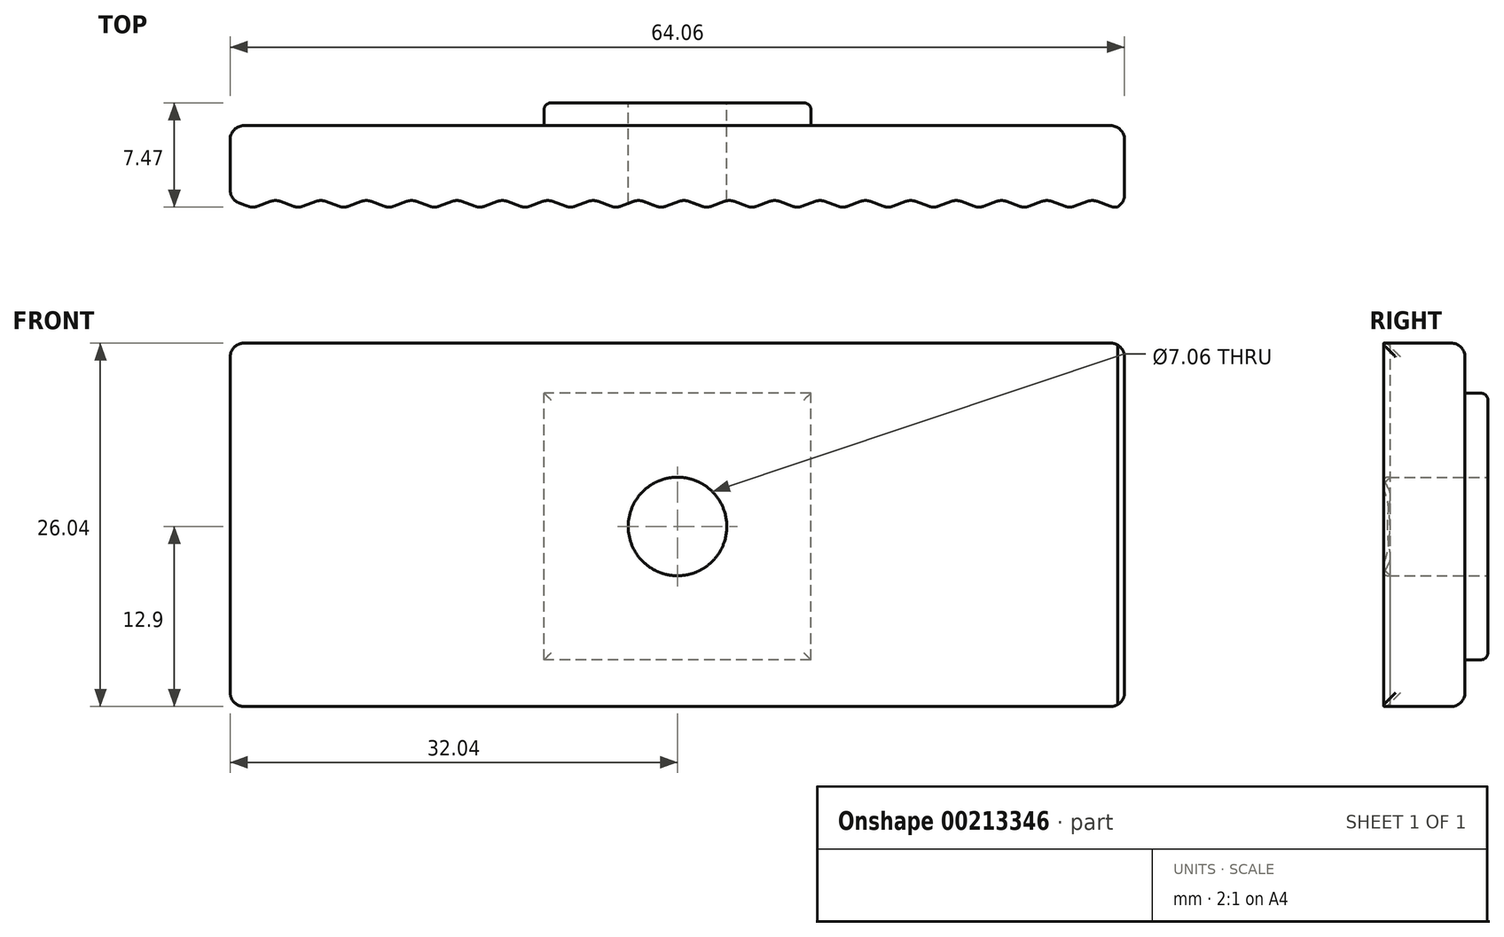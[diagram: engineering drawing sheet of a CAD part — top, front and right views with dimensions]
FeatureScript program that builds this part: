
annotation { "Feature Type Name" : "Feature", "Feature Type Description" : "" }
export const myFeature = defineFeature(function(context is Context, id is Id, definition is map)
    precondition{}
    {
        {
            var Q0;
            Q0=qCreatedBy(makeId("Front.planeOp"),FACE);
            var sketch = newSketch(context, id + "F0", { "sketchPlane" : qUnion([Q0])});
            skLineSegment(sketch, "E0.bottom", {"start": v(0, 0) * mm, "end": v(64.06, 0) * mm});
            skLineSegment(sketch, "E0.top", {"start": v(0, 26.04) * mm, "end": v(64.06, 26.04) * mm});
            skLineSegment(sketch, "E0.left", {"start": v(0, 0) * mm, "end": v(0, 26.04) * mm});
            skLineSegment(sketch, "E0.right", {"start": v(64.06, 0) * mm, "end": v(64.06, 26.04) * mm});
            skCircle(sketch, "E1", {"center": v(32.04, 12.9) * mm, "radius": 3.53 * mm});
            skSolve(sketch);
        }
        {
            var Q0;
            Q0 = qSketchRegion(id + "F0", true);
            extrude(context, id + "F1", {"entities" : qUnion([Q0]), "depth" : 5.3 * mm});
        }
        {
            var Q0;
            Q0=makeQuery(id+"F1.opExtrude","CAP_FACE",FACE,{"disambiguationData":[OSD([sQuery(id+"F0.wireOp",EDGE,"E0.bottom"),sQuery(id+"F0.wireOp",EDGE,"E0.top"),sQuery(id+"F0.wireOp",EDGE,"E0.left"),sQuery(id+"F0.wireOp",EDGE,"E0.right"),sQuery(id+"F0.wireOp",EDGE,"E1")])],"isStart":true});
            var sketch = newSketch(context, id + "F2", { "sketchPlane" : qUnion([Q0])});
            skLineSegment(sketch, "E2.bottom", {"start": v(-41.6, 3.35) * mm, "end": v(-22.48, 3.35) * mm});
            skLineSegment(sketch, "E2.top", {"start": v(-41.6, 22.46) * mm, "end": v(-22.48, 22.46) * mm});
            skLineSegment(sketch, "E2.left", {"start": v(-41.6, 3.35) * mm, "end": v(-41.6, 22.46) * mm});
            skLineSegment(sketch, "E2.right", {"start": v(-22.48, 3.35) * mm, "end": v(-22.49, 22.46) * mm});
            skCircle(sketch, "E3.0", {"center": v(-32.04, 12.9) * mm, "radius": 3.53 * mm});
            skSolve(sketch);
        }
        {
            var Q0;
            Q0 = qSketchRegion(id + "F2", true);
            extrude(context, id + "F3", {"entities" : qUnion([Q0]), "operationType" : NewBodyOperationType.ADD, "depth" : 1.64 * mm});
        }
        {
            var Q0;
            Q0=makeQuery(id+"F1.opExtrude","SWEPT_FACE",FACE,{"disambiguationData":[OSD([sQuery(id+"F0.wireOp",EDGE,"E0.top")])]});
            var sketch = newSketch(context, id + "F4", { "sketchPlane" : qUnion([Q0])});
            skLineSegment(sketch, "E4", {"start": v(0, -5.3) * mm, "end": v(1.63, -5.9) * mm});
            skLineSegment(sketch, "E5", {"start": v(1.62, -5.9) * mm, "end": v(3.25, -5.3) * mm});
            skLineSegment(sketch, "E6.1.0.0", {"start": v(3.25, -5.3) * mm, "end": v(4.88, -5.9) * mm});
            skLineSegment(sketch, "E6.1.0.1", {"start": v(4.87, -5.9) * mm, "end": v(6.5, -5.3) * mm});
            skLineSegment(sketch, "E6.2.0.0", {"start": v(6.5, -5.3) * mm, "end": v(8.12, -5.9) * mm});
            skLineSegment(sketch, "E6.2.0.1", {"start": v(8.12, -5.9) * mm, "end": v(9.75, -5.3) * mm});
            skLineSegment(sketch, "E6.3.0.0", {"start": v(9.75, -5.3) * mm, "end": v(11.38, -5.9) * mm});
            skLineSegment(sketch, "E6.3.0.1", {"start": v(11.38, -5.9) * mm, "end": v(13, -5.3) * mm});
            skLineSegment(sketch, "E6.4.0.0", {"start": v(13, -5.3) * mm, "end": v(14.63, -5.9) * mm});
            skLineSegment(sketch, "E6.4.0.1", {"start": v(14.62, -5.9) * mm, "end": v(16.25, -5.3) * mm});
            skLineSegment(sketch, "E6.5.0.0", {"start": v(16.25, -5.3) * mm, "end": v(17.88, -5.9) * mm});
            skLineSegment(sketch, "E6.5.0.1", {"start": v(17.88, -5.9) * mm, "end": v(19.5, -5.3) * mm});
            skLineSegment(sketch, "E6.6.0.0", {"start": v(19.5, -5.3) * mm, "end": v(21.13, -5.9) * mm});
            skLineSegment(sketch, "E6.6.0.1", {"start": v(21.12, -5.9) * mm, "end": v(22.75, -5.3) * mm});
            skLineSegment(sketch, "E6.7.0.0", {"start": v(22.75, -5.3) * mm, "end": v(24.38, -5.9) * mm});
            skLineSegment(sketch, "E6.7.0.1", {"start": v(24.38, -5.9) * mm, "end": v(26, -5.3) * mm});
            skLineSegment(sketch, "E6.8.0.0", {"start": v(26, -5.3) * mm, "end": v(27.63, -5.9) * mm});
            skLineSegment(sketch, "E6.8.0.1", {"start": v(27.62, -5.9) * mm, "end": v(29.25, -5.3) * mm});
            skLineSegment(sketch, "E6.9.0.0", {"start": v(29.25, -5.3) * mm, "end": v(30.88, -5.9) * mm});
            skLineSegment(sketch, "E6.9.0.1", {"start": v(30.88, -5.9) * mm, "end": v(32.5, -5.3) * mm});
            skLineSegment(sketch, "E6.10.0.0", {"start": v(32.5, -5.3) * mm, "end": v(34.12, -5.9) * mm});
            skLineSegment(sketch, "E6.10.0.1", {"start": v(34.12, -5.9) * mm, "end": v(35.75, -5.3) * mm});
            skLineSegment(sketch, "E6.11.0.0", {"start": v(35.75, -5.3) * mm, "end": v(37.38, -5.9) * mm});
            skLineSegment(sketch, "E6.11.0.1", {"start": v(37.38, -5.9) * mm, "end": v(39, -5.3) * mm});
            skLineSegment(sketch, "E6.12.0.0", {"start": v(39, -5.3) * mm, "end": v(40.63, -5.9) * mm});
            skLineSegment(sketch, "E6.12.0.1", {"start": v(40.62, -5.9) * mm, "end": v(42.25, -5.3) * mm});
            skLineSegment(sketch, "E6.13.0.0", {"start": v(42.25, -5.3) * mm, "end": v(43.88, -5.9) * mm});
            skLineSegment(sketch, "E6.13.0.1", {"start": v(43.88, -5.9) * mm, "end": v(45.5, -5.3) * mm});
            skLineSegment(sketch, "E6.14.0.0", {"start": v(45.5, -5.3) * mm, "end": v(47.13, -5.9) * mm});
            skLineSegment(sketch, "E6.14.0.1", {"start": v(47.12, -5.9) * mm, "end": v(48.75, -5.3) * mm});
            skLineSegment(sketch, "E6.15.0.0", {"start": v(48.75, -5.3) * mm, "end": v(50.38, -5.9) * mm});
            skLineSegment(sketch, "E6.15.0.1", {"start": v(50.37, -5.9) * mm, "end": v(52, -5.3) * mm});
            skLineSegment(sketch, "E6.16.0.0", {"start": v(52, -5.3) * mm, "end": v(53.63, -5.9) * mm});
            skLineSegment(sketch, "E6.16.0.1", {"start": v(53.62, -5.9) * mm, "end": v(55.25, -5.3) * mm});
            skLineSegment(sketch, "E6.17.0.0", {"start": v(55.25, -5.3) * mm, "end": v(56.88, -5.9) * mm});
            skLineSegment(sketch, "E6.17.0.1", {"start": v(56.88, -5.9) * mm, "end": v(58.5, -5.3) * mm});
            skLineSegment(sketch, "E6.18.0.0", {"start": v(58.5, -5.3) * mm, "end": v(60.13, -5.9) * mm});
            skLineSegment(sketch, "E6.18.0.1", {"start": v(60.12, -5.9) * mm, "end": v(61.75, -5.3) * mm});
            skLineSegment(sketch, "E6.19.0.0", {"start": v(61.75, -5.3) * mm, "end": v(63.38, -5.9) * mm});
            skLineSegment(sketch, "E6.19.0.1", {"start": v(63.38, -5.9) * mm, "end": v(64.06, -5.65) * mm});
            skLineSegment(sketch, "E6.direction1", {"start": v(0, -5.3) * mm, "end": v(3.25, -5.3) * mm, "construction": true});
            skLineSegment(sketch, "E7", {"start": v(0, -5.3) * mm, "end": v(0, -4.8) * mm});
            skLineSegment(sketch, "E8", {"start": v(0, -4.8) * mm, "end": v(64.06, -4.8) * mm});
            skLineSegment(sketch, "E9", {"start": v(64.06, -4.8) * mm, "end": v(64.06, -5.65) * mm});
            skPoint(sketch, "E10.orphan", {"position": v(65, -5.3) * mm});
            skSolve(sketch);
        }
        {
            var Q0;
            Q0 = qSketchRegion(id + "F4", true);
            var Q1;
            Q1=makeQuery(id+"F1.opExtrude","SWEPT_FACE",FACE,{"disambiguationData":[OSD([sQuery(id+"F0.wireOp",EDGE,"E0.bottom")])]});
            extrude(context, id + "F5", {"entities" : qUnion([Q0]), "operationType" : NewBodyOperationType.ADD, "endBound" : BoundingType.UP_TO_SURFACE, "oppositeDirection" : true, "endBoundEntityFace" : qUnion([Q1]), "depth" : 25 * mm});
        }
        {
            var Q0;
            Q0=makeQuery(id+"F5.opExtrude","SWEPT_EDGE",EDGE,{"disambiguationData":[OSD([sQuery(id+"F4.wireOp",EDGE,"E4"),sQuery(id+"F4.wireOp",EDGE,"E5")])]});
            var Q1;
            Q1=makeQuery(id+"F5.opExtrude","SWEPT_EDGE",EDGE,{"disambiguationData":[OSD([sQuery(id+"F0.wireOp",EDGE,"E0.top"),sQuery(id+"F4.wireOp",EDGE,"E5"),sQuery(id+"F4.wireOp",EDGE,"E6.1.0.0")])]});
            var Q2;
            Q2=makeQuery(id+"F5.opExtrude","SWEPT_EDGE",EDGE,{"disambiguationData":[OSD([sQuery(id+"F4.wireOp",EDGE,"E6.1.0.0"),sQuery(id+"F4.wireOp",EDGE,"E6.1.0.1")])]});
            var Q3;
            Q3=makeQuery(id+"F5.opExtrude","SWEPT_EDGE",EDGE,{"disambiguationData":[OSD([sQuery(id+"F0.wireOp",EDGE,"E0.top"),sQuery(id+"F4.wireOp",EDGE,"E6.1.0.1"),sQuery(id+"F4.wireOp",EDGE,"E6.2.0.0")])]});
            var Q4;
            Q4=makeQuery(id+"F5.opExtrude","SWEPT_EDGE",EDGE,{"disambiguationData":[OSD([sQuery(id+"F4.wireOp",EDGE,"E6.2.0.0"),sQuery(id+"F4.wireOp",EDGE,"E6.2.0.1")])]});
            var Q5;
            Q5=makeQuery(id+"F5.opExtrude","SWEPT_EDGE",EDGE,{"disambiguationData":[OSD([sQuery(id+"F0.wireOp",EDGE,"E0.top"),sQuery(id+"F4.wireOp",EDGE,"E6.2.0.1"),sQuery(id+"F4.wireOp",EDGE,"E6.3.0.0")])]});
            var Q6;
            Q6=makeQuery(id+"F5.opExtrude","SWEPT_EDGE",EDGE,{"disambiguationData":[OSD([sQuery(id+"F4.wireOp",EDGE,"E6.3.0.0"),sQuery(id+"F4.wireOp",EDGE,"E6.3.0.1")])]});
            var Q7;
            Q7=makeQuery(id+"F5.opExtrude","SWEPT_EDGE",EDGE,{"disambiguationData":[OSD([sQuery(id+"F0.wireOp",EDGE,"E0.top"),sQuery(id+"F4.wireOp",EDGE,"E6.3.0.1"),sQuery(id+"F4.wireOp",EDGE,"E6.4.0.0")])]});
            var Q8;
            Q8=makeQuery(id+"F5.opExtrude","SWEPT_EDGE",EDGE,{"disambiguationData":[OSD([sQuery(id+"F4.wireOp",EDGE,"E6.4.0.0"),sQuery(id+"F4.wireOp",EDGE,"E6.4.0.1")])]});
            var Q9;
            Q9=makeQuery(id+"F5.opExtrude","SWEPT_EDGE",EDGE,{"disambiguationData":[OSD([sQuery(id+"F0.wireOp",EDGE,"E0.top"),sQuery(id+"F4.wireOp",EDGE,"E6.4.0.1"),sQuery(id+"F4.wireOp",EDGE,"E6.5.0.0")])]});
            var Q10;
            Q10=makeQuery(id+"F5.opExtrude","SWEPT_EDGE",EDGE,{"disambiguationData":[OSD([sQuery(id+"F4.wireOp",EDGE,"E6.5.0.0"),sQuery(id+"F4.wireOp",EDGE,"E6.5.0.1")])]});
            var Q11;
            Q11=makeQuery(id+"F5.opExtrude","SWEPT_EDGE",EDGE,{"disambiguationData":[OSD([sQuery(id+"F0.wireOp",EDGE,"E0.top"),sQuery(id+"F4.wireOp",EDGE,"E6.5.0.1"),sQuery(id+"F4.wireOp",EDGE,"E6.6.0.0")])]});
            var Q12;
            Q12=makeQuery(id+"F5.opExtrude","SWEPT_EDGE",EDGE,{"disambiguationData":[OSD([sQuery(id+"F4.wireOp",EDGE,"E6.6.0.0"),sQuery(id+"F4.wireOp",EDGE,"E6.6.0.1")])]});
            var Q13;
            Q13=makeQuery(id+"F5.opExtrude","SWEPT_EDGE",EDGE,{"disambiguationData":[OSD([sQuery(id+"F0.wireOp",EDGE,"E0.top"),sQuery(id+"F4.wireOp",EDGE,"E6.6.0.1"),sQuery(id+"F4.wireOp",EDGE,"E6.7.0.0")])]});
            var Q14;
            Q14=makeQuery(id+"F5.opExtrude","SWEPT_EDGE",EDGE,{"disambiguationData":[OSD([sQuery(id+"F4.wireOp",EDGE,"E6.7.0.0"),sQuery(id+"F4.wireOp",EDGE,"E6.7.0.1")])]});
            var Q15;
            Q15=makeQuery(id+"F5.opExtrude","SWEPT_EDGE",EDGE,{"disambiguationData":[OSD([sQuery(id+"F0.wireOp",EDGE,"E0.top"),sQuery(id+"F4.wireOp",EDGE,"E6.7.0.1"),sQuery(id+"F4.wireOp",EDGE,"E6.8.0.0")])]});
            var Q16;
            Q16=makeQuery(id+"F5.opExtrude","SWEPT_EDGE",EDGE,{"disambiguationData":[OSD([sQuery(id+"F4.wireOp",EDGE,"E6.8.0.0"),sQuery(id+"F4.wireOp",EDGE,"E6.8.0.1")])]});
            var Q17;
            Q17=makeQuery(id+"F5.opExtrude","SWEPT_EDGE",EDGE,{"disambiguationData":[OSD([sQuery(id+"F0.wireOp",EDGE,"E0.top"),sQuery(id+"F4.wireOp",EDGE,"E6.8.0.1"),sQuery(id+"F4.wireOp",EDGE,"E6.9.0.0")])]});
            var Q18;
            Q18=makeQuery(id+"F5.opExtrude","SWEPT_EDGE",EDGE,{"disambiguationData":[OSD([sQuery(id+"F4.wireOp",EDGE,"E6.9.0.0"),sQuery(id+"F4.wireOp",EDGE,"E6.9.0.1")])]});
            var Q19;
            Q19=makeQuery(id+"F5.opExtrude","SWEPT_EDGE",EDGE,{"disambiguationData":[OSD([sQuery(id+"F0.wireOp",EDGE,"E0.top"),sQuery(id+"F4.wireOp",EDGE,"E6.9.0.1"),sQuery(id+"F4.wireOp",EDGE,"E6.10.0.0")])]});
            var Q20;
            Q20=makeQuery(id+"F5.opExtrude","SWEPT_EDGE",EDGE,{"disambiguationData":[OSD([sQuery(id+"F4.wireOp",EDGE,"E6.10.0.0"),sQuery(id+"F4.wireOp",EDGE,"E6.10.0.1")])]});
            var Q21;
            Q21=makeQuery(id+"F5.opExtrude","SWEPT_EDGE",EDGE,{"disambiguationData":[OSD([sQuery(id+"F0.wireOp",EDGE,"E0.top"),sQuery(id+"F4.wireOp",EDGE,"E6.10.0.1"),sQuery(id+"F4.wireOp",EDGE,"E6.11.0.0")])]});
            var Q22;
            Q22=makeQuery(id+"F5.opExtrude","SWEPT_EDGE",EDGE,{"disambiguationData":[OSD([sQuery(id+"F4.wireOp",EDGE,"E6.11.0.0"),sQuery(id+"F4.wireOp",EDGE,"E6.11.0.1")])]});
            var Q23;
            Q23=makeQuery(id+"F5.opExtrude","SWEPT_EDGE",EDGE,{"disambiguationData":[OSD([sQuery(id+"F0.wireOp",EDGE,"E0.top"),sQuery(id+"F4.wireOp",EDGE,"E6.11.0.1"),sQuery(id+"F4.wireOp",EDGE,"E6.12.0.0")])]});
            var Q24;
            Q24=makeQuery(id+"F5.opExtrude","SWEPT_EDGE",EDGE,{"disambiguationData":[OSD([sQuery(id+"F4.wireOp",EDGE,"E6.12.0.0"),sQuery(id+"F4.wireOp",EDGE,"E6.12.0.1")])]});
            var Q25;
            Q25=makeQuery(id+"F5.opExtrude","SWEPT_EDGE",EDGE,{"disambiguationData":[OSD([sQuery(id+"F0.wireOp",EDGE,"E0.top"),sQuery(id+"F4.wireOp",EDGE,"E6.12.0.1"),sQuery(id+"F4.wireOp",EDGE,"E6.13.0.0")])]});
            var Q26;
            Q26=makeQuery(id+"F5.opExtrude","SWEPT_EDGE",EDGE,{"disambiguationData":[OSD([sQuery(id+"F4.wireOp",EDGE,"E6.13.0.0"),sQuery(id+"F4.wireOp",EDGE,"E6.13.0.1")])]});
            var Q27;
            Q27=makeQuery(id+"F5.opExtrude","SWEPT_EDGE",EDGE,{"disambiguationData":[OSD([sQuery(id+"F0.wireOp",EDGE,"E0.top"),sQuery(id+"F4.wireOp",EDGE,"E6.13.0.1"),sQuery(id+"F4.wireOp",EDGE,"E6.14.0.0")])]});
            var Q28;
            Q28=makeQuery(id+"F5.opExtrude","SWEPT_EDGE",EDGE,{"disambiguationData":[OSD([sQuery(id+"F4.wireOp",EDGE,"E6.14.0.0"),sQuery(id+"F4.wireOp",EDGE,"E6.14.0.1")])]});
            var Q29;
            Q29=makeQuery(id+"F5.opExtrude","SWEPT_EDGE",EDGE,{"disambiguationData":[OSD([sQuery(id+"F0.wireOp",EDGE,"E0.top"),sQuery(id+"F4.wireOp",EDGE,"E6.14.0.1"),sQuery(id+"F4.wireOp",EDGE,"E6.15.0.0")])]});
            var Q30;
            Q30=makeQuery(id+"F5.opExtrude","SWEPT_EDGE",EDGE,{"disambiguationData":[OSD([sQuery(id+"F4.wireOp",EDGE,"E6.15.0.0"),sQuery(id+"F4.wireOp",EDGE,"E6.15.0.1")])]});
            var Q31;
            Q31=makeQuery(id+"F5.opExtrude","SWEPT_EDGE",EDGE,{"disambiguationData":[OSD([sQuery(id+"F0.wireOp",EDGE,"E0.top"),sQuery(id+"F4.wireOp",EDGE,"E6.15.0.1"),sQuery(id+"F4.wireOp",EDGE,"E6.16.0.0")])]});
            var Q32;
            Q32=makeQuery(id+"F5.opExtrude","SWEPT_EDGE",EDGE,{"disambiguationData":[OSD([sQuery(id+"F4.wireOp",EDGE,"E6.16.0.0"),sQuery(id+"F4.wireOp",EDGE,"E6.16.0.1")])]});
            var Q33;
            Q33=makeQuery(id+"F5.opExtrude","SWEPT_EDGE",EDGE,{"disambiguationData":[OSD([sQuery(id+"F0.wireOp",EDGE,"E0.top"),sQuery(id+"F4.wireOp",EDGE,"E6.16.0.1"),sQuery(id+"F4.wireOp",EDGE,"E6.17.0.0")])]});
            var Q34;
            Q34=makeQuery(id+"F5.opExtrude","SWEPT_EDGE",EDGE,{"disambiguationData":[OSD([sQuery(id+"F4.wireOp",EDGE,"E6.17.0.0"),sQuery(id+"F4.wireOp",EDGE,"E6.17.0.1")])]});
            var Q35;
            Q35=makeQuery(id+"F5.opExtrude","SWEPT_EDGE",EDGE,{"disambiguationData":[OSD([sQuery(id+"F0.wireOp",EDGE,"E0.top"),sQuery(id+"F4.wireOp",EDGE,"E6.17.0.1"),sQuery(id+"F4.wireOp",EDGE,"E6.18.0.0")])]});
            var Q36;
            Q36=makeQuery(id+"F5.opExtrude","SWEPT_EDGE",EDGE,{"disambiguationData":[OSD([sQuery(id+"F4.wireOp",EDGE,"E6.18.0.0"),sQuery(id+"F4.wireOp",EDGE,"E6.18.0.1")])]});
            var Q37;
            Q37=makeQuery(id+"F5.opExtrude","SWEPT_EDGE",EDGE,{"disambiguationData":[OSD([sQuery(id+"F0.wireOp",EDGE,"E0.top"),sQuery(id+"F4.wireOp",EDGE,"E6.18.0.1"),sQuery(id+"F4.wireOp",EDGE,"E6.19.0.0")])]});
            var Q38;
            Q38=makeQuery(id+"F5.opExtrude","SWEPT_EDGE",EDGE,{"disambiguationData":[OSD([sQuery(id+"F4.wireOp",EDGE,"E6.19.0.0"),sQuery(id+"F4.wireOp",EDGE,"E6.19.0.1")])]});
            var Q39;
            Q39=makeQuery(id+"F5.opExtrude","SWEPT_EDGE",EDGE,{"disambiguationData":[OSD([sQuery(id+"F4.wireOp",EDGE,"E6.19.0.1"),sQuery(id+"F4.wireOp",EDGE,"E9")])]});
            var Q40;
            Q40=makeQuery(id+"F5.boolean.opBoolean","MERGE",EDGE,{"derivedFrom":[makeQuery(id+"F1.opExtrude","CAP_EDGE",EDGE,{"disambiguationData":[OSD([sQuery(id+"F0.wireOp",EDGE,"E0.left")])],"isStart":false}),makeQuery(id+"F5.opExtrude","SWEPT_EDGE",EDGE,{"disambiguationData":[OSD([sQuery(id+"F0.wireOp",EDGE,"E0.top"),sQuery(id+"F4.wireOp",EDGE,"E4"),sQuery(id+"F4.wireOp",EDGE,"E7")])]})]});
            var Q41;
            Q41=makeQuery(id+"F1.opExtrude","SWEPT_EDGE",EDGE,{"disambiguationData":[OSD([sQuery(id+"F0.wireOp",EDGE,"E0.bottom"),sQuery(id+"F0.wireOp",EDGE,"E0.left")])]});
            var Q42;
            {var subQ0=sQuery(id+"F4.wireOp",EDGE,"E9");var subQ1=sQuery(id+"F0.wireOp",EDGE,"E0.top");var subQ3=sQuery(id+"F0.wireOp",EDGE,"E0.right");var subQ4=sQuery(id+"F0.wireOp",EDGE,"E0.bottom");Q42=makeQuery(id+"F5.boolean.opBoolean","MERGE",EDGE,{"derivedFrom":[makeQuery(id+"F1.opExtrude","SWEPT_EDGE",EDGE,{"disambiguationData":[OSD([subQ4,subQ3])]}),makeQuery(id+"F5.opExtrude","TWEAK_EDGE",EDGE,{"derivedFrom":[makeQuery(id+"F1.opExtrude","SWEPT_FACE",FACE,{"disambiguationData":[OSD([subQ4])]}),makeQuery(id+"F4.imprint","IMPRINT",EDGE,{"disambiguationData":[TD([[makeQuery(id+"F4.imprint","INTERSECT",VERTEX,{"derivedFrom":[sQuery(id+"F4.wireOp",EDGE,"E6.19.0.1"),subQ0]}),1.0]])],"derivedFrom":subQ0}),makeQuery(id+"F4.imprint","IMPRINT",EDGE,{"disambiguationData":[TD([[makeQuery(id+"F4.imprint","INTERSECT",VERTEX,{"derivedFrom":[makeQuery(id+"F1.opExtrude","SWEPT_EDGE",EDGE,{"disambiguationData":[OSD([subQ1,subQ3])]}),sQuery(id+"F4.wireOp",EDGE,"E8"),subQ0]}),1.0]])],"derivedFrom":subQ0})]})]});}
            var Q43;
            Q43=makeQuery(id+"F1.opExtrude","SWEPT_EDGE",EDGE,{"disambiguationData":[OSD([sQuery(id+"F0.wireOp",EDGE,"E0.top"),sQuery(id+"F0.wireOp",EDGE,"E0.left")])]});
            var Q44;
            Q44=makeQuery(id+"F5.boolean.opBoolean","MERGE",EDGE,{"derivedFrom":[makeQuery(id+"F1.opExtrude","SWEPT_EDGE",EDGE,{"disambiguationData":[OSD([sQuery(id+"F0.wireOp",EDGE,"E0.top"),sQuery(id+"F0.wireOp",EDGE,"E0.right")])]}),makeQuery(id+"F5.opExtrude","CAP_EDGE",EDGE,{"disambiguationData":[OSD([sQuery(id+"F4.wireOp",EDGE,"E9")])],"isStart":true})]});
            var Q45;
            Q45=makeQuery(id+"F1.opExtrude","CAP_EDGE",EDGE,{"disambiguationData":[OSD([sQuery(id+"F0.wireOp",EDGE,"E0.top")])],"isStart":true});
            var Q46;
            Q46=makeQuery(id+"F1.opExtrude","CAP_EDGE",EDGE,{"disambiguationData":[OSD([sQuery(id+"F0.wireOp",EDGE,"E0.right")])],"isStart":true});
            var Q47;
            Q47=makeQuery(id+"F1.opExtrude","CAP_EDGE",EDGE,{"disambiguationData":[OSD([sQuery(id+"F0.wireOp",EDGE,"E0.bottom")])],"isStart":true});
            var Q48;
            Q48=makeQuery(id+"F1.opExtrude","CAP_EDGE",EDGE,{"disambiguationData":[OSD([sQuery(id+"F0.wireOp",EDGE,"E0.left")])],"isStart":true});
            fillet(context, id + "F6", {"entities" : qUnion([Q0, Q1, Q2, Q3, Q4, Q5, Q6, Q7, Q8, Q9, Q10, Q11, Q12, Q13, Q14, Q15, Q16, Q17, Q18, Q19, Q20, Q21, Q22, Q23, Q24, Q25, Q26, Q27, Q28, Q29, Q30, Q31, Q32, Q33, Q34, Q35, Q36, Q37, Q38, Q39, Q40, Q41, Q42, Q43, Q44, Q45, Q46, Q47, Q48]), "radius" : 1 * mm, "tangentPropagation" : true, "allowEdgeOverflow" : false});
        }
        {
            var Q0;
            Q0=makeQuery(id+"F3.opExtrude","CAP_EDGE",EDGE,{"disambiguationData":[OSD([sQuery(id+"F2.wireOp",EDGE,"E2.top")])],"isStart":true});
            var Q1;
            Q1=makeQuery(id+"F3.opExtrude","CAP_EDGE",EDGE,{"disambiguationData":[OSD([sQuery(id+"F2.wireOp",EDGE,"E2.right")])],"isStart":true});
            var Q2;
            Q2=makeQuery(id+"F3.opExtrude","CAP_EDGE",EDGE,{"disambiguationData":[OSD([sQuery(id+"F2.wireOp",EDGE,"E2.top")])],"isStart":false});
            var Q3;
            Q3=makeQuery(id+"F3.opExtrude","CAP_EDGE",EDGE,{"disambiguationData":[OSD([sQuery(id+"F2.wireOp",EDGE,"E2.right")])],"isStart":false});
            var Q4;
            Q4=makeQuery(id+"F3.opExtrude","CAP_EDGE",EDGE,{"disambiguationData":[OSD([sQuery(id+"F2.wireOp",EDGE,"E2.left")])],"isStart":false});
            var Q5;
            Q5=makeQuery(id+"F3.opExtrude","CAP_EDGE",EDGE,{"disambiguationData":[OSD([sQuery(id+"F2.wireOp",EDGE,"E2.bottom")])],"isStart":false});
            var Q6;
            Q6=makeQuery(id+"F3.opExtrude","CAP_EDGE",EDGE,{"disambiguationData":[OSD([sQuery(id+"F2.wireOp",EDGE,"E2.left")])],"isStart":true});
            var Q7;
            Q7=makeQuery(id+"F3.opExtrude","CAP_EDGE",EDGE,{"disambiguationData":[OSD([sQuery(id+"F2.wireOp",EDGE,"E2.bottom")])],"isStart":true});
            fillet(context, id + "F7", {"entities" : qUnion([Q0, Q1, Q2, Q3, Q4, Q5, Q6, Q7]), "radius" : .5 * mm, "tangentPropagation" : true, "allowEdgeOverflow" : false});
        }
        {
            var Q0;
            Q0=makeQuery(id+"F5.opExtrude","SWEPT_FACE",FACE,{"disambiguationData":[OSD([sQuery(id+"F4.wireOp",EDGE,"E8")])]});
            var sketch = newSketch(context, id + "F8", { "sketchPlane" : qUnion([Q0])});
            skCircle(sketch, "E11.0", {"center": v(-32.04, 12.9) * mm, "radius": 3.53 * mm});
            skSolve(sketch);
        }
        {
            var Q0;
            Q0 = qSketchRegion(id + "F8", true);
            extrude(context, id + "F9", {"entities" : qUnion([Q0]), "operationType" : NewBodyOperationType.REMOVE, "oppositeDirection" : true, "depth" : 25 * mm});
        }
    });
